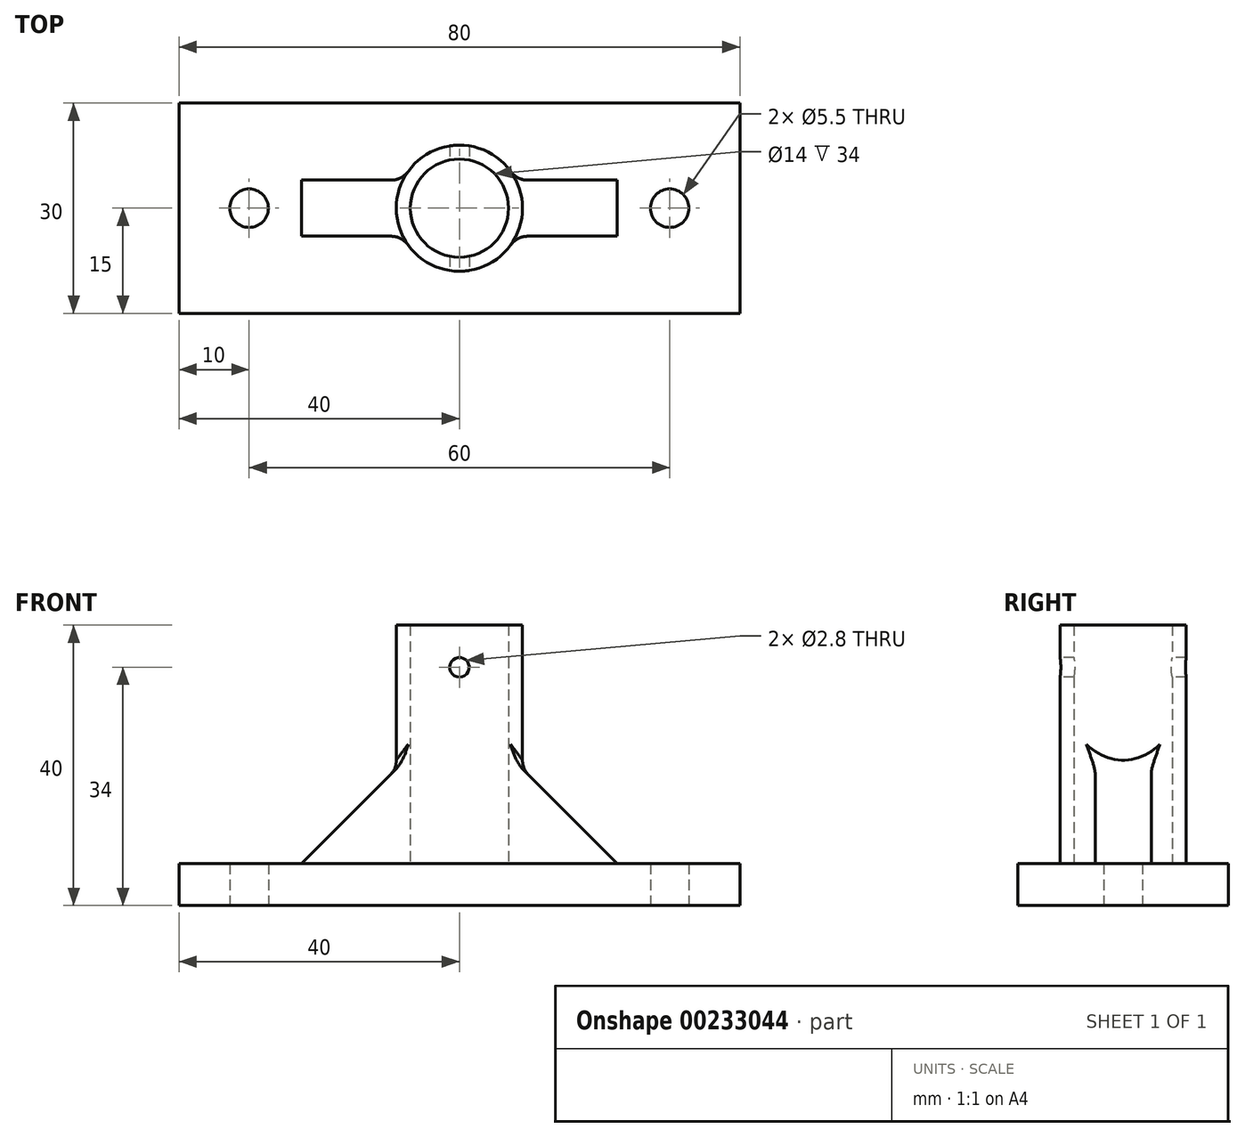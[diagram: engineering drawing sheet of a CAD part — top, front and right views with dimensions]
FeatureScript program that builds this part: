
annotation { "Feature Type Name" : "Feature", "Feature Type Description" : "" }
export const myFeature = defineFeature(function(context is Context, id is Id, definition is map)
    precondition{}
    {
        {
            var Q0;
            Q0=qCreatedBy(makeId("Top.planeOp"),FACE);
            var sketch = newSketch(context, id + "F0", { "sketchPlane" : qUnion([Q0])});
            skLineSegment(sketch, "E0.bottom", {"start": v(-40, -15) * mm, "end": v(40, -15) * mm});
            skLineSegment(sketch, "E0.top", {"start": v(-40, 15) * mm, "end": v(40, 15) * mm});
            skLineSegment(sketch, "E0.left", {"start": v(-40, -15) * mm, "end": v(-40, 15) * mm});
            skLineSegment(sketch, "E0.right", {"start": v(40, -15) * mm, "end": v(40, 15) * mm});
            skCircle(sketch, "E1", {"center": v(-30, 0) * mm, "radius": 2.75 * mm});
            skCircle(sketch, "E2", {"center": v(30, 0) * mm, "radius": 2.75 * mm});
            skSolve(sketch);
        }
        {
            var Q0;
            Q0=makeQuery(id+"F0.imprint","IMPRINT",FACE,{"disambiguationData":[TD([[makeQuery(id+"F0.imprint","IMPRINT",EDGE,{"derivedFrom":sQuery(id+"F0.wireOp",EDGE,"E0.bottom")}),1.0]])]});
            extrude(context, id + "F1", {"entities" : qUnion([Q0]), "depth" : 6 * mm});
        }
        {
            var Q0;
            Q0=makeQuery(id+"F1.opExtrude","CAP_FACE",FACE,{"disambiguationData":[OSD([sQuery(id+"F0.wireOp",EDGE,"E0.bottom"),sQuery(id+"F0.wireOp",EDGE,"E0.top"),sQuery(id+"F0.wireOp",EDGE,"E0.left"),sQuery(id+"F0.wireOp",EDGE,"E0.right"),sQuery(id+"F0.wireOp",EDGE,"E1"),sQuery(id+"F0.wireOp",EDGE,"E2")])],"isStart":false});
            var sketch = newSketch(context, id + "F2", { "sketchPlane" : qUnion([Q0])});
            skCircle(sketch, "E3", {"center": v(0, 0) * mm, "radius": 7 * mm});
            skCircle(sketch, "E4", {"center": v(0, 0) * mm, "radius": 9 * mm});
            skSolve(sketch);
        }
        {
            var Q0;
            Q0=makeQuery(id+"F2.imprint","IMPRINT",FACE,{"disambiguationData":[TD([[makeQuery(id+"F2.imprint","IMPRINT",EDGE,{"derivedFrom":sQuery(id+"F2.wireOp",EDGE,"E3")}),-1.0]])]});
            extrude(context, id + "F3", {"entities" : qUnion([Q0]), "operationType" : NewBodyOperationType.ADD, "depth" : 34 * mm});
        }
        {
            var Q0;
            Q0=qCreatedBy(makeId("Front.planeOp"),FACE);
            var sketch = newSketch(context, id + "F4", { "sketchPlane" : qUnion([Q0])});
            skLineSegment(sketch, "E5", {"start": v(-22.5, 6) * mm, "end": v(-7.5, 6) * mm});
            skLineSegment(sketch, "E6", {"start": v(-7.5, 6) * mm, "end": v(-7.5, 21) * mm});
            skLineSegment(sketch, "E7", {"start": v(-7.5, 21) * mm, "end": v(-22.5, 6) * mm});
            skLineSegment(sketch, "E8", {"start": v(7.5, 21) * mm, "end": v(22.5, 6) * mm});
            skLineSegment(sketch, "E9", {"start": v(22.5, 6) * mm, "end": v(7.5, 6) * mm});
            skLineSegment(sketch, "E10", {"start": v(7.5, 6) * mm, "end": v(7.5, 21) * mm});
            skSolve(sketch);
        }
        {
            var Q0;
            Q0=makeQuery(id+"F4.imprint","IMPRINT",FACE,{"disambiguationData":[TD([[makeQuery(id+"F4.imprint","IMPRINT",EDGE,{"derivedFrom":sQuery(id+"F4.wireOp",EDGE,"E5")}),1.0]])]});
            var Q1;
            Q1=makeQuery(id+"F4.imprint","IMPRINT",FACE,{"disambiguationData":[TD([[makeQuery(id+"F4.imprint","IMPRINT",EDGE,{"derivedFrom":sQuery(id+"F4.wireOp",EDGE,"E8")}),-1.0]])]});
            extrude(context, id + "F5", {"entities" : qUnion([Q0, Q1]), "operationType" : NewBodyOperationType.ADD, "endBound" : BoundingType.SYMMETRIC, "depth" : 8 * mm});
        }
        {
            var Q0;
            Q0=makeQuery(id+"F5.opExtrude","SWEPT_EDGE",EDGE,{"disambiguationData":[OSD([sQuery(id+"F4.wireOp",EDGE,"E5"),sQuery(id+"F4.wireOp",EDGE,"E7")])]});
            var Q1;
            Q1=makeQuery(id+"F5.opExtrude","CAP_EDGE",EDGE,{"disambiguationData":[OSD([sQuery(id+"F4.wireOp",EDGE,"E5")])],"isStart":false});
            var Q2;
            {var subQ0=sQuery(id+"F2.wireOp",EDGE,"E4");Q2=makeQuery(id+"F5.boolean.opBoolean","SPLIT",EDGE,{"disambiguationData":[TD([makeQuery(id+"F5.opExtrude","CAP_FACE",FACE,{"disambiguationData":[OSD([sQuery(id+"F4.wireOp",EDGE,"E5"),sQuery(id+"F4.wireOp",EDGE,"E6"),sQuery(id+"F4.wireOp",EDGE,"E7")])],"isStart":false})])],"derivedFrom":makeQuery(id+"F3.opExtrude","CAP_EDGE",EDGE,{"disambiguationData":[OSD([subQ0])],"isStart":true})});}
            var Q3;
            Q3=makeQuery(id+"F5.opExtrude","CAP_EDGE",EDGE,{"disambiguationData":[OSD([sQuery(id+"F4.wireOp",EDGE,"E9")])],"isStart":false});
            var Q4;
            Q4=makeQuery(id+"F5.opExtrude","SWEPT_EDGE",EDGE,{"disambiguationData":[OSD([sQuery(id+"F4.wireOp",EDGE,"E8"),sQuery(id+"F4.wireOp",EDGE,"E9")])]});
            var Q5;
            Q5=makeQuery(id+"F5.opExtrude","CAP_EDGE",EDGE,{"disambiguationData":[OSD([sQuery(id+"F4.wireOp",EDGE,"E9")])],"isStart":true});
            var Q6;
            {var subQ0=sQuery(id+"F2.wireOp",EDGE,"E4");Q6=makeQuery(id+"F5.boolean.opBoolean","SPLIT",EDGE,{"disambiguationData":[TD([makeQuery(id+"F5.opExtrude","CAP_FACE",FACE,{"disambiguationData":[OSD([sQuery(id+"F4.wireOp",EDGE,"E5"),sQuery(id+"F4.wireOp",EDGE,"E6"),sQuery(id+"F4.wireOp",EDGE,"E7")])],"isStart":true})])],"derivedFrom":makeQuery(id+"F3.opExtrude","CAP_EDGE",EDGE,{"disambiguationData":[OSD([subQ0])],"isStart":true})});}
            var Q7;
            Q7=makeQuery(id+"F5.opExtrude","CAP_EDGE",EDGE,{"disambiguationData":[OSD([sQuery(id+"F4.wireOp",EDGE,"E5")])],"isStart":true});
            var Q8;
            Q8=makeQuery(id+"F5.boolean.opBoolean","INTERSECT",EDGE,{"derivedFrom":[makeQuery(id+"F3.opExtrude","SWEPT_FACE",FACE,{"disambiguationData":[OSD([sQuery(id+"F2.wireOp",EDGE,"E4")])]}),makeQuery(id+"F5.opExtrude","SWEPT_FACE",FACE,{"disambiguationData":[OSD([sQuery(id+"F4.wireOp",EDGE,"E7")])]})]});
            var Q9;
            Q9=makeQuery(id+"F5.boolean.opBoolean","INTERSECT",EDGE,{"derivedFrom":[makeQuery(id+"F3.opExtrude","SWEPT_FACE",FACE,{"disambiguationData":[OSD([sQuery(id+"F2.wireOp",EDGE,"E4")])]}),makeQuery(id+"F5.opExtrude","CAP_FACE",FACE,{"disambiguationData":[OSD([sQuery(id+"F4.wireOp",EDGE,"E5"),sQuery(id+"F4.wireOp",EDGE,"E6"),sQuery(id+"F4.wireOp",EDGE,"E7")])],"isStart":false})]});
            var Q10;
            Q10=makeQuery(id+"F5.boolean.opBoolean","INTERSECT",EDGE,{"derivedFrom":[makeQuery(id+"F3.opExtrude","SWEPT_FACE",FACE,{"disambiguationData":[OSD([sQuery(id+"F2.wireOp",EDGE,"E4")])]}),makeQuery(id+"F5.opExtrude","CAP_FACE",FACE,{"disambiguationData":[OSD([sQuery(id+"F4.wireOp",EDGE,"E5"),sQuery(id+"F4.wireOp",EDGE,"E6"),sQuery(id+"F4.wireOp",EDGE,"E7")])],"isStart":true})]});
            var Q11;
            Q11=makeQuery(id+"F5.boolean.opBoolean","INTERSECT",EDGE,{"derivedFrom":[makeQuery(id+"F3.opExtrude","SWEPT_FACE",FACE,{"disambiguationData":[OSD([sQuery(id+"F2.wireOp",EDGE,"E4")])]}),makeQuery(id+"F5.opExtrude","SWEPT_FACE",FACE,{"disambiguationData":[OSD([sQuery(id+"F4.wireOp",EDGE,"E8")])]})]});
            var Q12;
            Q12=makeQuery(id+"F5.boolean.opBoolean","INTERSECT",EDGE,{"derivedFrom":[makeQuery(id+"F3.opExtrude","SWEPT_FACE",FACE,{"disambiguationData":[OSD([sQuery(id+"F2.wireOp",EDGE,"E4")])]}),makeQuery(id+"F5.opExtrude","CAP_FACE",FACE,{"disambiguationData":[OSD([sQuery(id+"F4.wireOp",EDGE,"E8"),sQuery(id+"F4.wireOp",EDGE,"E9"),sQuery(id+"F4.wireOp",EDGE,"E10")])],"isStart":true})]});
            var Q13;
            Q13=makeQuery(id+"F5.boolean.opBoolean","INTERSECT",EDGE,{"derivedFrom":[makeQuery(id+"F3.opExtrude","SWEPT_FACE",FACE,{"disambiguationData":[OSD([sQuery(id+"F2.wireOp",EDGE,"E4")])]}),makeQuery(id+"F5.opExtrude","CAP_FACE",FACE,{"disambiguationData":[OSD([sQuery(id+"F4.wireOp",EDGE,"E8"),sQuery(id+"F4.wireOp",EDGE,"E9"),sQuery(id+"F4.wireOp",EDGE,"E10")])],"isStart":false})]});
            fillet(context, id + "F6", {"entities" : qUnion([Q0, Q1, Q2, Q3, Q4, Q5, Q6, Q7, Q8, Q9, Q10, Q11, Q12, Q13]), "radius" : 3 * mm, "tangentPropagation" : true, "allowEdgeOverflow" : false});
        }
        {
            var Q0;
            Q0=qCreatedBy(makeId("Front.planeOp"),FACE);
            var sketch = newSketch(context, id + "F7", { "sketchPlane" : qUnion([Q0])});
            skCircle(sketch, "E11", {"center": v(0, 34) * mm, "radius": 1.4 * mm});
            skSolve(sketch);
        }
        {
            var Q0;
            Q0=makeQuery(id+"F7.imprint","IMPRINT",FACE,{"disambiguationData":[TD([[makeQuery(id+"F7.imprint","IMPRINT",EDGE,{"derivedFrom":sQuery(id+"F7.wireOp",EDGE,"E11")}),1.0]])]});
            extrude(context, id + "F8", {"entities" : qUnion([Q0]), "operationType" : NewBodyOperationType.REMOVE, "endBound" : BoundingType.SYMMETRIC, "oppositeDirection" : true, "depth" : 25 * mm});
        }
    });
